# Revit family: Haworth_Openest_SingleBooth
name_source: partatom
category: Furniture
revit_build: Autodesk Revit 2018 (Build: 20170223_1515(x64)
units: mm (PartAtom-declared; Revit-internal decimal feet)

## family parameters
Always vertical = Yes
Cut with Voids When Loaded = No
OmniClass Number = 23.40.20.00
OmniClass Title = General Furniture and Specialties
Room Calculation Point = No
Shared = No
Work Plane-Based = No

## types (1)
- HOAB
    Actual Depth = 5' - 5 1/4"
    Actual Width = 2' - 5"
    Assembly Code = E2020200
    CoatHook = No
    Description = Haworth - Openest - Single Bench
    Height Adjustable Table = No
    Hideaway Power Module = No
    Manufacturer = Haworth
    Model = Openest
    Pillow = Yes
    Power Location = 0' - 0"
    Rectangular Pillow = No
    Revision No. = 2
    Square Pillow = Yes
    Sustainability Info = https://www.haworth.com
    URL = http://www.haworth.com
    URL - Product = https://www.haworth.com
    Warranty = http://www.haworth.com

## geometry (parser evidence)
native form markers: Sweep x16
no freeform markers — native parametric forms only
